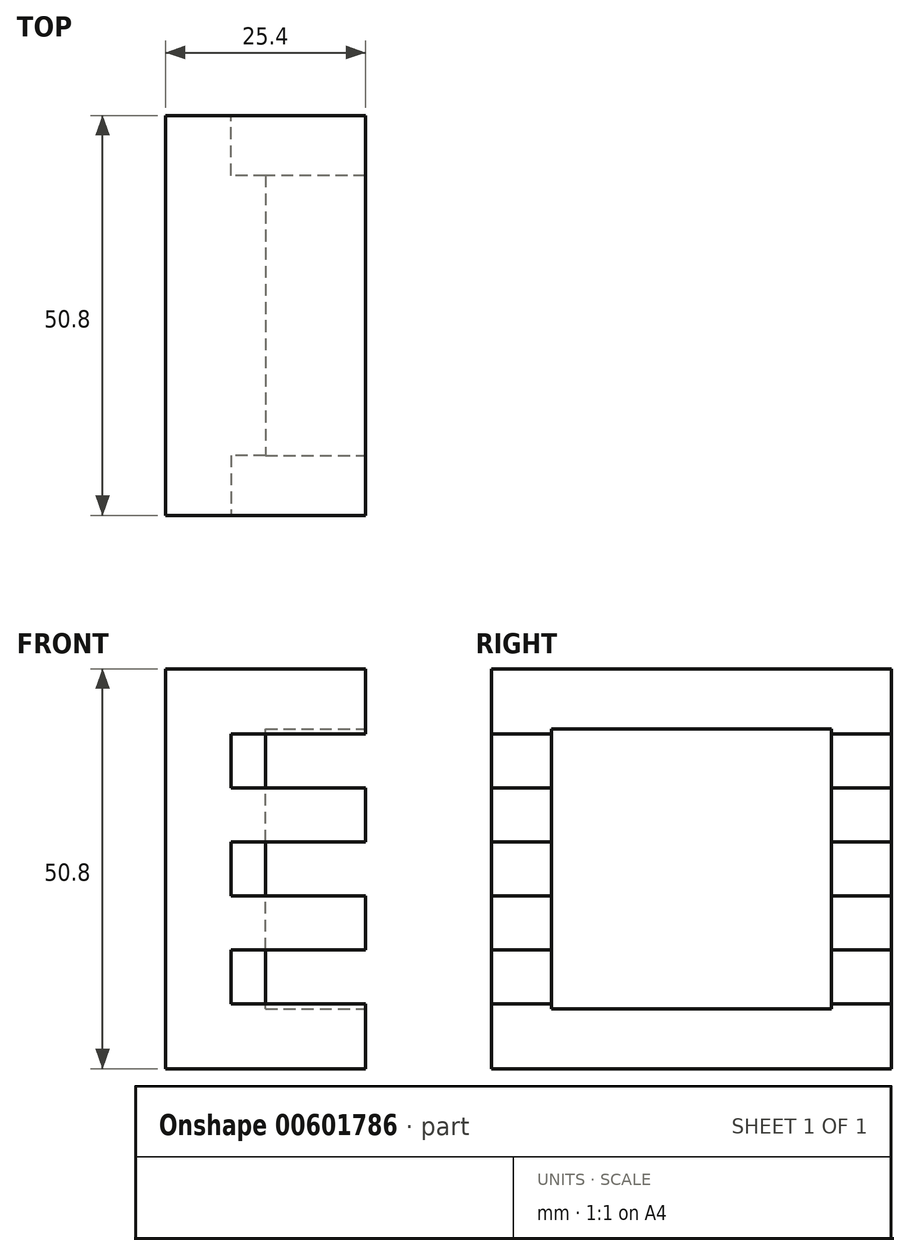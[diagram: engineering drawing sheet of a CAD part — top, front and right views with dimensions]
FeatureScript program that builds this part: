
annotation { "Feature Type Name" : "Feature", "Feature Type Description" : "" }
export const myFeature = defineFeature(function(context is Context, id is Id, definition is map)
    precondition{}
    {
        {
            var Q0;
            Q0=qCreatedBy(makeId("Front.planeOp"),FACE);
            var sketch = newSketch(context, id + "F0", { "sketchPlane" : qUnion([Q0])});
            skLineSegment(sketch, "E0", {"start": v(0, 0) * mm, "end": v(0, 50.8) * mm});
            skLineSegment(sketch, "E1", {"start": v(0, 50.8) * mm, "end": v(25.4, 50.8) * mm});
            skLineSegment(sketch, "E2", {"start": v(25.4, 50.8) * mm, "end": v(25.4, 0) * mm});
            skLineSegment(sketch, "E3", {"start": v(25.4, 0) * mm, "end": v(0, 0) * mm});
            skSolve(sketch);
        }
        {
            var Q0;
            Q0=makeQuery(id+"F0.imprint","IMPRINT",FACE,{"disambiguationData":[TD([[makeQuery(id+"F0.imprint","IMPRINT",EDGE,{"derivedFrom":sQuery(id+"F0.wireOp",EDGE,"E0")}),-1.0]])]});
            extrude(context, id + "F1", {"entities" : qUnion([Q0]), "depth" : 50.8 * mm, "offsetDistance" : 25.4 * mm});
        }
        {
            var Q0;
            Q0=makeQuery(id+"F1.opExtrude","SWEPT_FACE",FACE,{"disambiguationData":[OSD([sQuery(id+"F0.wireOp",EDGE,"E2")])]});
            var sketch = newSketch(context, id + "F2", { "sketchPlane" : qUnion([Q0])});
            skLineSegment(sketch, "E4", {"start": v(-43.18, 43.18) * mm, "end": v(-43.18, 7.62) * mm});
            skLineSegment(sketch, "E5", {"start": v(-43.18, 7.62) * mm, "end": v(-7.62, 7.62) * mm});
            skLineSegment(sketch, "E6", {"start": v(-7.62, 7.62) * mm, "end": v(-7.62, 43.18) * mm});
            skLineSegment(sketch, "E7", {"start": v(-7.62, 43.18) * mm, "end": v(-43.18, 43.18) * mm});
            skSolve(sketch);
        }
        {
            var Q0;
            Q0=makeQuery(id+"F2.imprint","IMPRINT",FACE,{"disambiguationData":[TD([[makeQuery(id+"F2.imprint","IMPRINT",EDGE,{"derivedFrom":sQuery(id+"F2.wireOp",EDGE,"E4")}),1.0]])]});
            extrude(context, id + "F3", {"entities" : qUnion([Q0]), "operationType" : NewBodyOperationType.REMOVE, "oppositeDirection" : true, "depth" : 12.7 * mm, "offsetDistance" : 25.4 * mm});
        }
        {
            var Q0;
            Q0=makeQuery(id+"F1.opExtrude","CAP_FACE",FACE,{"disambiguationData":[OSD([sQuery(id+"F0.wireOp",EDGE,"E0"),sQuery(id+"F0.wireOp",EDGE,"E1"),sQuery(id+"F0.wireOp",EDGE,"E2"),sQuery(id+"F0.wireOp",EDGE,"E3")])],"isStart":false});
            var sketch = newSketch(context, id + "F4", { "sketchPlane" : qUnion([Q0])});
            skLineSegment(sketch, "E8", {"start": v(25.4, 42.55) * mm, "end": v(8.31, 42.55) * mm});
            skLineSegment(sketch, "E9", {"start": v(8.31, 42.55) * mm, "end": v(8.31, 35.69) * mm});
            skLineSegment(sketch, "E10", {"start": v(8.31, 35.69) * mm, "end": v(25.4, 35.69) * mm});
            skLineSegment(sketch, "E11", {"start": v(25.4, 28.83) * mm, "end": v(8.31, 28.83) * mm});
            skLineSegment(sketch, "E12", {"start": v(8.31, 28.83) * mm, "end": v(8.31, 21.97) * mm});
            skLineSegment(sketch, "E13", {"start": v(8.31, 21.97) * mm, "end": v(25.4, 21.97) * mm});
            skLineSegment(sketch, "E14", {"start": v(25.4, 15.11) * mm, "end": v(8.31, 15.11) * mm});
            skLineSegment(sketch, "E15", {"start": v(8.31, 15.11) * mm, "end": v(8.31, 8.25) * mm});
            skLineSegment(sketch, "E16", {"start": v(8.31, 8.25) * mm, "end": v(25.4, 8.25) * mm});
            skLineSegment(sketch, "E17", {"start": v(25.4, 42.55) * mm, "end": v(25.4, 35.69) * mm});
            skLineSegment(sketch, "E18", {"start": v(25.4, 28.83) * mm, "end": v(25.4, 21.97) * mm});
            skLineSegment(sketch, "E19", {"start": v(25.4, 15.11) * mm, "end": v(25.4, 8.25) * mm});
            skSolve(sketch);
        }
        {
            var Q0;
            Q0=makeQuery(id+"F4.imprint","IMPRINT",FACE,{"disambiguationData":[TD([[makeQuery(id+"F4.imprint","IMPRINT",EDGE,{"derivedFrom":sQuery(id+"F4.wireOp",EDGE,"E8")}),1.0]])]});
            var Q1;
            Q1=makeQuery(id+"F4.imprint","IMPRINT",FACE,{"disambiguationData":[TD([[makeQuery(id+"F4.imprint","IMPRINT",EDGE,{"derivedFrom":sQuery(id+"F4.wireOp",EDGE,"E11")}),1.0]])]});
            var Q2;
            Q2=makeQuery(id+"F4.imprint","IMPRINT",FACE,{"disambiguationData":[TD([[makeQuery(id+"F4.imprint","IMPRINT",EDGE,{"derivedFrom":sQuery(id+"F4.wireOp",EDGE,"E14")}),1.0]])]});
            extrude(context, id + "F5", {"entities" : qUnion([Q0, Q1, Q2]), "operationType" : NewBodyOperationType.REMOVE, "oppositeDirection" : true, "depth" : 7.62 * mm, "offsetDistance" : 25.4 * mm});
        }
        {
            var Q0;
            Q0=makeQuery(id+"F1.opExtrude","CAP_FACE",FACE,{"disambiguationData":[OSD([sQuery(id+"F0.wireOp",EDGE,"E0"),sQuery(id+"F0.wireOp",EDGE,"E1"),sQuery(id+"F0.wireOp",EDGE,"E2"),sQuery(id+"F0.wireOp",EDGE,"E3")])],"isStart":true});
            var sketch = newSketch(context, id + "F6", { "sketchPlane" : qUnion([Q0])});
            skLineSegment(sketch, "E20", {"start": v(-25.4, 42.55) * mm, "end": v(-8.3, 42.55) * mm});
            skLineSegment(sketch, "E21", {"start": v(-8.3, 42.54) * mm, "end": v(-8.3, 35.69) * mm});
            skLineSegment(sketch, "E22", {"start": v(-8.3, 35.69) * mm, "end": v(-25.4, 35.69) * mm});
            skLineSegment(sketch, "E23", {"start": v(-25.4, 35.69) * mm, "end": v(-25.4, 42.55) * mm});
            skLineSegment(sketch, "E24", {"start": v(-25.4, 28.83) * mm, "end": v(-8.3, 28.83) * mm});
            skLineSegment(sketch, "E25", {"start": v(-8.3, 28.83) * mm, "end": v(-8.3, 21.97) * mm});
            skLineSegment(sketch, "E26", {"start": v(-8.3, 21.97) * mm, "end": v(-25.4, 21.97) * mm});
            skLineSegment(sketch, "E27", {"start": v(-25.4, 21.97) * mm, "end": v(-25.4, 28.83) * mm});
            skLineSegment(sketch, "E28", {"start": v(-25.4, 15.11) * mm, "end": v(-8.3, 15.11) * mm});
            skLineSegment(sketch, "E29", {"start": v(-8.3, 15.11) * mm, "end": v(-8.3, 8.26) * mm});
            skLineSegment(sketch, "E30", {"start": v(-8.3, 8.26) * mm, "end": v(-25.4, 8.26) * mm});
            skLineSegment(sketch, "E31", {"start": v(-25.4, 8.26) * mm, "end": v(-25.4, 15.11) * mm});
            skSolve(sketch);
        }
        {
            var Q0;
            Q0 = qSketchRegion(id + "F6", true);
            extrude(context, id + "F7", {"entities" : qUnion([Q0]), "operationType" : NewBodyOperationType.REMOVE, "oppositeDirection" : true, "depth" : 7.62 * mm, "offsetDistance" : 25.4 * mm});
        }
    });
